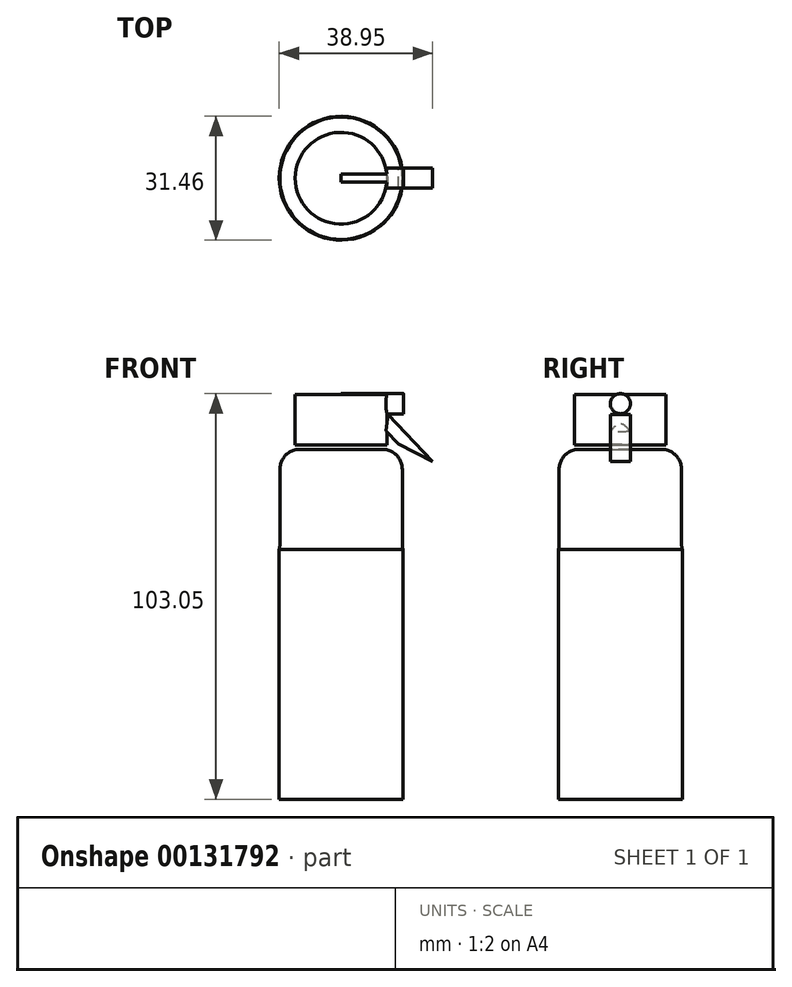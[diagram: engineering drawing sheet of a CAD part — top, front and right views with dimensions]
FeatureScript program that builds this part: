
annotation { "Feature Type Name" : "Feature", "Feature Type Description" : "" }
export const myFeature = defineFeature(function(context is Context, id is Id, definition is map)
    precondition{}
    {
        {
            var Q0;
            Q0=qCreatedBy(makeId("Top.planeOp"),FACE);
            var sketch = newSketch(context, id + "F0", { "sketchPlane" : qUnion([Q0])});
            skCircle(sketch, "E0", {"center": v(0, 0) * mm, "radius": 15.73 * mm});
            skSolve(sketch);
        }
        {
            var Q0;
            Q0 = qSketchRegion(id + "F0", true);
            extrude(context, id + "F1", {"entities" : qUnion([Q0]), "depth" : 63.5 * mm});
        }
        {
            var Q0;
            Q0=makeQuery(id+"F1.opExtrude","CAP_FACE",FACE,{"disambiguationData":[OSD([sQuery(id+"F0.wireOp",EDGE,"E0")])],"isStart":false});
            var sketch = newSketch(context, id + "F2", { "sketchPlane" : qUnion([Q0])});
            skCircle(sketch, "E1", {"center": v(0, 0) * mm, "radius": 15.55 * mm});
            skSolve(sketch);
        }
        {
            var Q0;
            Q0 = qSketchRegion(id + "F2", true);
            extrude(context, id + "F3", {"entities" : qUnion([Q0]), "operationType" : NewBodyOperationType.ADD, "depth" : 25.4 * mm});
        }
        {
            var Q0;
            Q0=makeQuery(id+"F3.opExtrude","CAP_FACE",FACE,{"disambiguationData":[OSD([sQuery(id+"F2.wireOp",EDGE,"E1")])],"isStart":false});
            var Q1;
            Q1=makeQuery(id+"F3.opExtrude","SWEPT_FACE",FACE,{"disambiguationData":[OSD([sQuery(id+"F2.wireOp",EDGE,"E1")])]});
            fillet(context, id + "F4", {"entities" : qUnion([Q0, Q1]), "radius" : 5.08 * mm, "tangentPropagation" : true, "allowEdgeOverflow" : false});
        }
        {
            var Q0;
            Q0=qCreatedBy(makeId("Front.planeOp"),FACE);
            var sketch = newSketch(context, id + "F5", { "sketchPlane" : qUnion([Q0])});
            skLineSegment(sketch, "E2", {"start": v(0, 87.43) * mm, "end": v(0, 118.26) * mm});
            skLineSegment(sketch, "E3", {"start": v(0, 102.85) * mm, "end": v(11.65, 102.85) * mm});
            skLineSegment(sketch, "E4", {"start": v(11.65, 102.85) * mm, "end": v(11.65, 89.94) * mm});
            skLineSegment(sketch, "E5", {"start": v(11.65, 89.94) * mm, "end": v(0, 89.94) * mm});
            skSolve(sketch);
        }
        {
            var Q0;
            Q0 = qSketchRegion(id + "F5", true);
            var Q1;
            Q1=sQuery(id+"F5.wireOp",EDGE,"E2");
            revolve(context, id + "F6", {"entities" : qUnion([Q0]), "axis" : qUnion([Q1]), "revolveType" : RevolveType.FULL});
        }
        {
            var Q0;
            Q0=qCreatedBy(makeId("Front.planeOp"),FACE);
            var sketch = newSketch(context, id + "F7", { "sketchPlane" : qUnion([Q0])});
            skLineSegment(sketch, "E6", {"start": v(11.97, 97.71) * mm, "end": v(23.22, 85.78) * mm});
            skLineSegment(sketch, "E7", {"start": v(23.22, 85.78) * mm, "end": v(14.64, 90.24) * mm});
            skLineSegment(sketch, "E8", {"start": v(14.64, 90.24) * mm, "end": v(11.4, 93.5) * mm});
            skLineSegment(sketch, "E9", {"start": v(11.97, 97.71) * mm, "end": v(11.4, 93.5) * mm});
            skSolve(sketch);
        }
        {
            var Q0;
            Q0=makeQuery(id+"F7.imprint","IMPRINT",FACE,{"disambiguationData":[TD([[makeQuery(id+"F7.imprint","IMPRINT",EDGE,{"derivedFrom":sQuery(id+"F7.wireOp",EDGE,"E6")}),-1.0]])]});
            extrude(context, id + "F8", {"entities" : qUnion([Q0]), "operationType" : NewBodyOperationType.ADD, "endBound" : BoundingType.SYMMETRIC, "depth" : 5.08 * mm});
        }
        {
            var Q0;
            Q0=qCreatedBy(makeId("Right.planeOp"),FACE);
            var sketch = newSketch(context, id + "F9", { "sketchPlane" : qUnion([Q0])});
            skCircle(sketch, "E10", {"center": v(0, 100.49) * mm, "radius": 2.56 * mm});
            skSolve(sketch);
        }
        {
            var Q0;
            Q0 = qSketchRegion(id + "F9", true);
            extrude(context, id + "F10", {"entities" : qUnion([Q0]), "operationType" : NewBodyOperationType.ADD, "depth" : 15.9 * mm});
        }
    });
